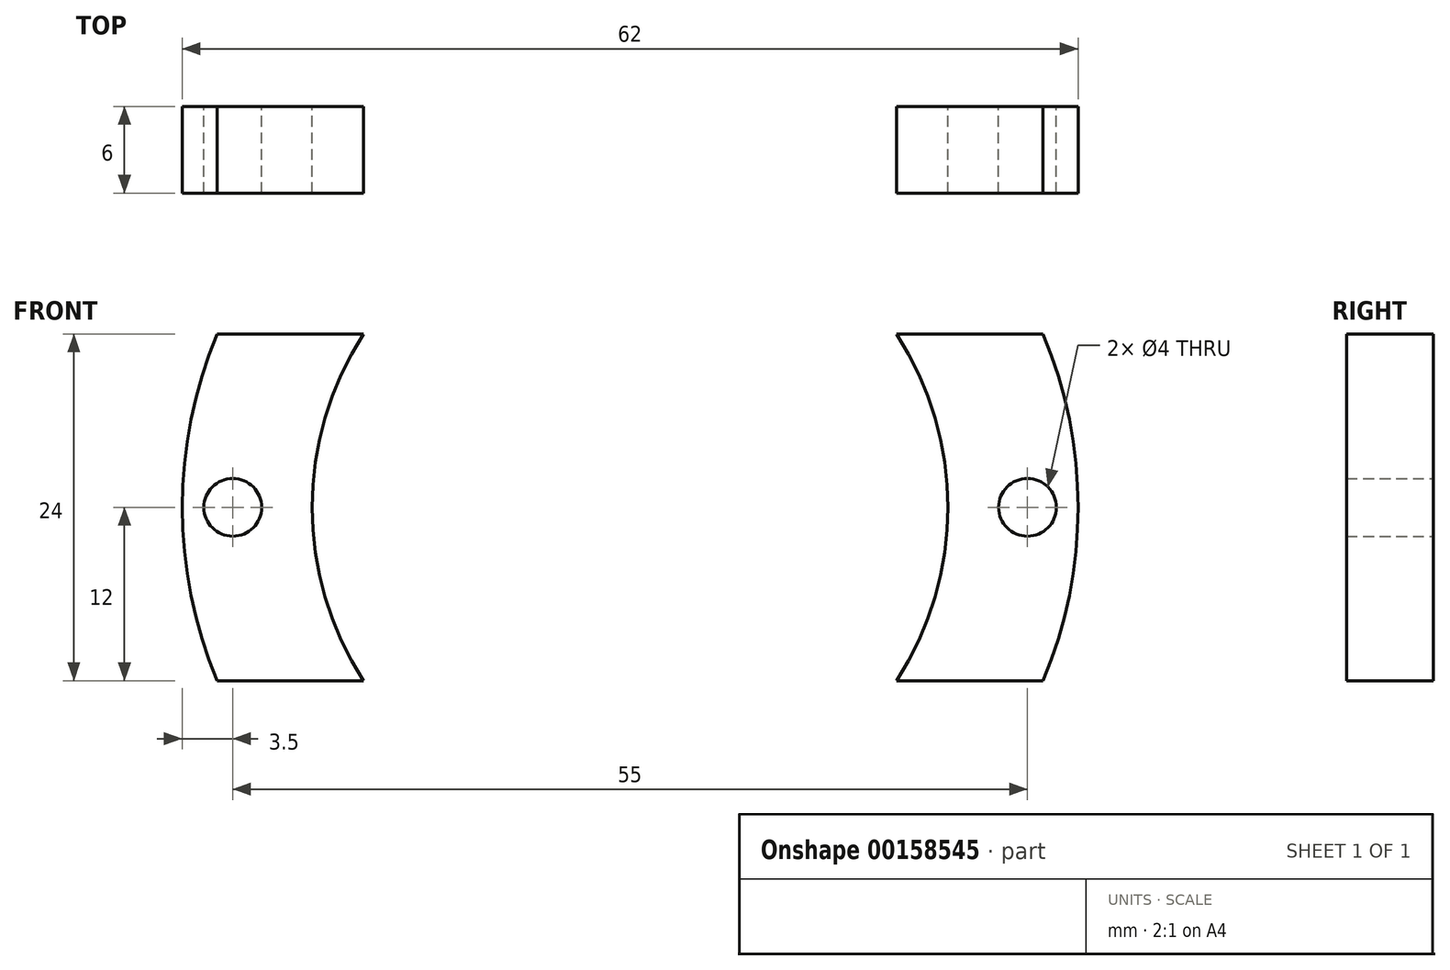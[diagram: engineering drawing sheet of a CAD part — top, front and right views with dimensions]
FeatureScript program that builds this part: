
annotation { "Feature Type Name" : "Feature", "Feature Type Description" : "" }
export const myFeature = defineFeature(function(context is Context, id is Id, definition is map)
    precondition{}
    {
        {
            var Q0;
            Q0=qCreatedBy(makeId("Front.planeOp"),FACE);
            var sketch = newSketch(context, id + "F0", { "sketchPlane" : qUnion([Q0])});
            skCircle(sketch, "E0", {"center": v(0, 0) * mm, "radius": 31 * mm});
            skCircle(sketch, "E1", {"center": v(0, 0) * mm, "radius": 22 * mm});
            skLineSegment(sketch, "E2", {"start": v(-28.58, 12) * mm, "end": v(28.58, 12) * mm});
            skLineSegment(sketch, "E3", {"start": v(28.58, -12) * mm, "end": v(-28.58, -12) * mm});
            skCircle(sketch, "E4", {"center": v(0, 0) * mm, "radius": 24.5 * mm});
            skCircle(sketch, "E5", {"center": v(-27.5, 0) * mm, "radius": 2 * mm});
            skCircle(sketch, "E6", {"center": v(27.5, 0) * mm, "radius": 2 * mm});
            skSolve(sketch);
        }
        {
            var Q0;
            Q0=makeQuery(id+"F0.imprint","IMPRINT",FACE,{"disambiguationData":[TD([[makeQuery(id+"F0.imprint","IMPRINT",EDGE,{"derivedFrom":sQuery(id+"F0.wireOp",EDGE,"E5")}),-1.0]])]});
            var Q1;
            Q1=makeQuery(id+"F0.imprint","IMPRINT",FACE,{"disambiguationData":[TD([[makeQuery(id+"F0.imprint","IMPRINT",EDGE,{"derivedFrom":sQuery(id+"F0.wireOp",EDGE,"E6")}),-1.0]])]});
            var Q2;
            {var subQ0=sQuery(id+"F0.wireOp",EDGE,"E2");var subQ1=sQuery(id+"F0.wireOp",EDGE,"E1");var subQ2=makeQuery(id+"F0.imprint","INTERSECT",VERTEX,{"disambiguationData":[OD(1.0)],"derivedFrom":[subQ1,subQ0]});Q2=makeQuery(id+"F0.imprint","IMPRINT",FACE,{"disambiguationData":[TD([[makeQuery(id+"F0.imprint","IMPRINT",EDGE,{"disambiguationData":[TD([[subQ2,1.0]])],"derivedFrom":subQ1}),-1.0]])]});}
            var Q3;
            {var subQ0=sQuery(id+"F0.wireOp",EDGE,"E2");var subQ1=sQuery(id+"F0.wireOp",EDGE,"E1");var subQ2=makeQuery(id+"F0.imprint","INTERSECT",VERTEX,{"disambiguationData":[OD(0.0)],"derivedFrom":[subQ1,subQ0]});Q3=makeQuery(id+"F0.imprint","IMPRINT",FACE,{"disambiguationData":[TD([[makeQuery(id+"F0.imprint","IMPRINT",EDGE,{"disambiguationData":[TD([[subQ2,-1.0]])],"derivedFrom":subQ1}),-1.0]])]});}
            extrude(context, id + "F1", {"entities" : qUnion([Q0, Q1, Q2, Q3]), "depth" : 6 * mm, "offsetDistance" : 25 * mm});
        }
    });
